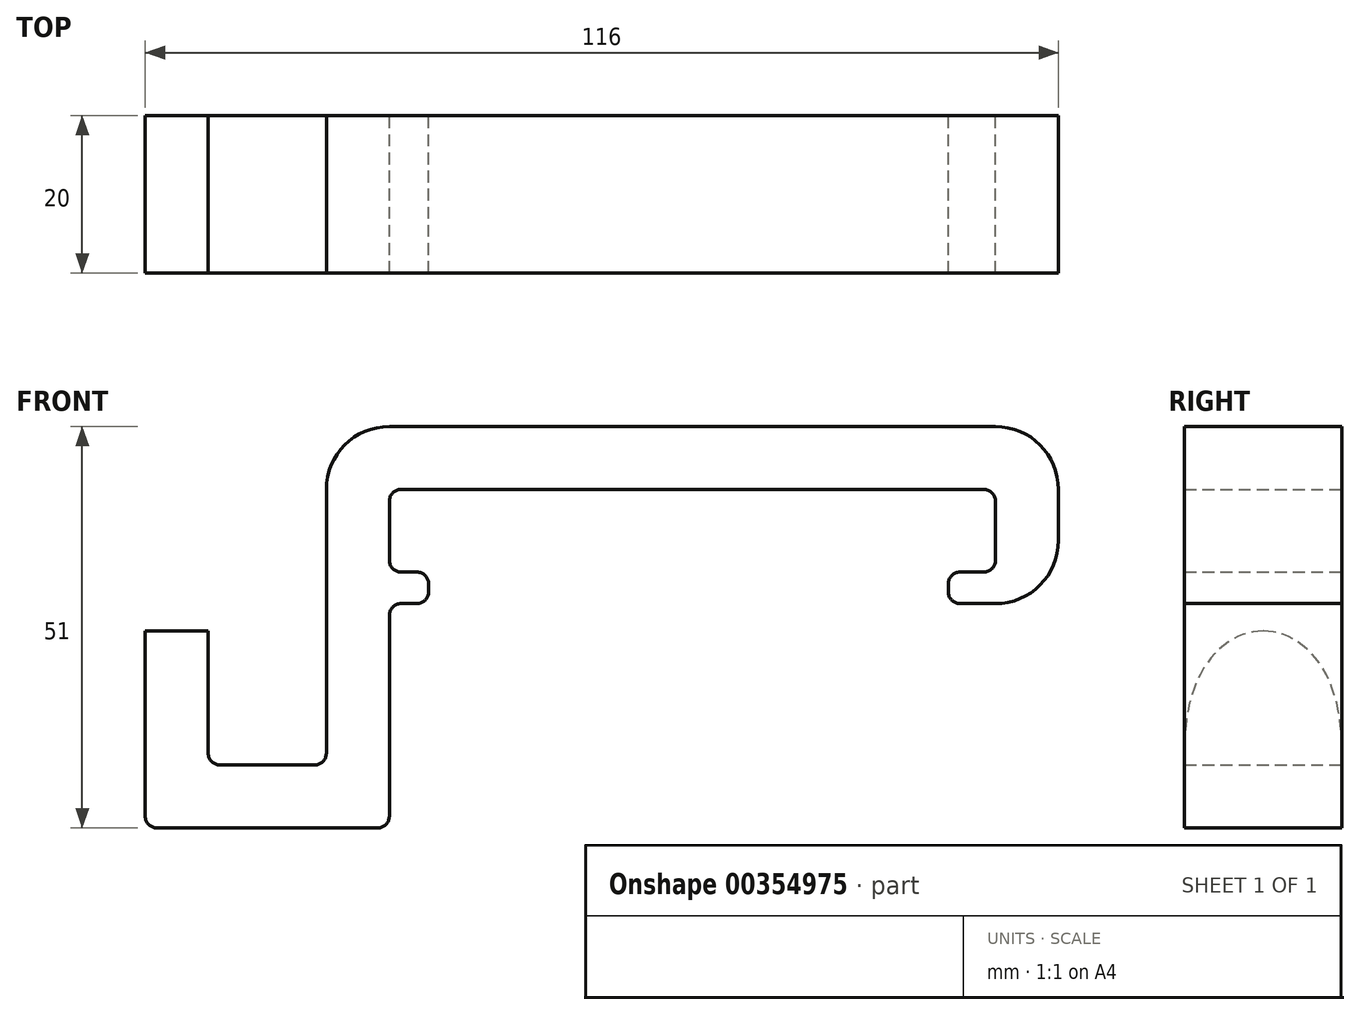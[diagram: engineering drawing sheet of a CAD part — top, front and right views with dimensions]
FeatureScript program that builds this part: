
annotation { "Feature Type Name" : "Feature", "Feature Type Description" : "" }
export const myFeature = defineFeature(function(context is Context, id is Id, definition is map)
    precondition{}
    {
        {
            var Q0;
            Q0=qCreatedBy(makeId("Front.planeOp"),FACE);
            var sketch = newSketch(context, id + "F0", { "sketchPlane" : qUnion([Q0])});
            skLineSegment(sketch, "E0", {"start": v(0, 0) * mm, "end": v(-77, 0) * mm});
            skLineSegment(sketch, "E1", {"start": v(-77, 0) * mm, "end": v(-77, -43) * mm});
            skLineSegment(sketch, "E2", {"start": v(-77, -43) * mm, "end": v(-108, -43) * mm});
            skLineSegment(sketch, "E3", {"start": v(-108, -43) * mm, "end": v(-108, -18) * mm});
            skLineSegment(sketch, "E4", {"start": v(-108, -18) * mm, "end": v(-100, -18) * mm});
            skLineSegment(sketch, "E5", {"start": v(-100, -18) * mm, "end": v(-100, -35) * mm});
            skLineSegment(sketch, "E6", {"start": v(-100, -35) * mm, "end": v(-85, -35) * mm});
            skLineSegment(sketch, "E7", {"start": v(-85, -35) * mm, "end": v(-85, 0) * mm});
            skLineSegment(sketch, "E8", {"start": v(-85, 0) * mm, "end": v(-85, 8) * mm});
            skLineSegment(sketch, "E9", {"start": v(-85, 8) * mm, "end": v(8, 8) * mm});
            skLineSegment(sketch, "E10", {"start": v(8, 8) * mm, "end": v(8, -14.5) * mm});
            skLineSegment(sketch, "E11", {"start": v(8, -14.5) * mm, "end": v(-6, -14.5) * mm});
            skLineSegment(sketch, "E12", {"start": v(-6, -14.5) * mm, "end": v(-6, -10.5) * mm});
            skLineSegment(sketch, "E13", {"start": v(-6, -10.5) * mm, "end": v(0, -10.5) * mm});
            skLineSegment(sketch, "E14", {"start": v(0, -10.5) * mm, "end": v(0, 0) * mm});
            skLineSegment(sketch, "E15", {"start": v(-77, -10.5) * mm, "end": v(-72, -10.5) * mm});
            skLineSegment(sketch, "E16", {"start": v(-72, -10.5) * mm, "end": v(-72, -14.5) * mm});
            skLineSegment(sketch, "E17", {"start": v(-72, -14.5) * mm, "end": v(-77, -14.5) * mm});
            skSolve(sketch);
        }
        {
            var Q0;
            Q0 = qSketchRegion(id + "F0", true);
            extrude(context, id + "F1", {"entities" : qUnion([Q0]), "depth" : 20 * mm});
        }
        {
            var Q0;
            Q0=makeQuery(id+"F1.opExtrude","SWEPT_EDGE",EDGE,{"disambiguationData":[OSD([sQuery(id+"F0.wireOp",EDGE,"E11"),sQuery(id+"F0.wireOp",EDGE,"E12")])]});
            var Q1;
            Q1=makeQuery(id+"F1.opExtrude","SWEPT_EDGE",EDGE,{"disambiguationData":[OSD([sQuery(id+"F0.wireOp",EDGE,"E12"),sQuery(id+"F0.wireOp",EDGE,"E13")])]});
            var Q2;
            Q2=makeQuery(id+"F1.opExtrude","SWEPT_EDGE",EDGE,{"disambiguationData":[OSD([sQuery(id+"F0.wireOp",EDGE,"E13"),sQuery(id+"F0.wireOp",EDGE,"E14")])]});
            var Q3;
            Q3=makeQuery(id+"F1.opExtrude","SWEPT_EDGE",EDGE,{"disambiguationData":[OSD([sQuery(id+"F0.wireOp",EDGE,"E0"),sQuery(id+"F0.wireOp",EDGE,"E14")])]});
            var Q4;
            Q4=makeQuery(id+"F1.opExtrude","SWEPT_EDGE",EDGE,{"disambiguationData":[OSD([sQuery(id+"F0.wireOp",EDGE,"E16"),sQuery(id+"F0.wireOp",EDGE,"E17")])]});
            var Q5;
            Q5=makeQuery(id+"F1.opExtrude","SWEPT_EDGE",EDGE,{"disambiguationData":[OSD([sQuery(id+"F0.wireOp",EDGE,"E15"),sQuery(id+"F0.wireOp",EDGE,"E16")])]});
            var Q6;
            Q6=makeQuery(id+"F1.opExtrude","SWEPT_EDGE",EDGE,{"disambiguationData":[OSD([sQuery(id+"F0.wireOp",EDGE,"E1"),sQuery(id+"F0.wireOp",EDGE,"E15")])]});
            var Q7;
            Q7=makeQuery(id+"F1.opExtrude","SWEPT_EDGE",EDGE,{"disambiguationData":[OSD([sQuery(id+"F0.wireOp",EDGE,"E1"),sQuery(id+"F0.wireOp",EDGE,"E17")])]});
            var Q8;
            Q8=makeQuery(id+"F1.opExtrude","SWEPT_EDGE",EDGE,{"disambiguationData":[OSD([sQuery(id+"F0.wireOp",EDGE,"E1"),sQuery(id+"F0.wireOp",EDGE,"E2")])]});
            var Q9;
            Q9=makeQuery(id+"F1.opExtrude","SWEPT_EDGE",EDGE,{"disambiguationData":[OSD([sQuery(id+"F0.wireOp",EDGE,"E2"),sQuery(id+"F0.wireOp",EDGE,"E3")])]});
            var Q10;
            Q10=makeQuery(id+"F1.opExtrude","SWEPT_EDGE",EDGE,{"disambiguationData":[OSD([sQuery(id+"F0.wireOp",EDGE,"E0"),sQuery(id+"F0.wireOp",EDGE,"E1")])]});
            var Q11;
            Q11=makeQuery(id+"F1.opExtrude","SWEPT_EDGE",EDGE,{"disambiguationData":[OSD([sQuery(id+"F0.wireOp",EDGE,"E6"),sQuery(id+"F0.wireOp",EDGE,"E7")])]});
            var Q12;
            Q12=makeQuery(id+"F1.opExtrude","SWEPT_EDGE",EDGE,{"disambiguationData":[OSD([sQuery(id+"F0.wireOp",EDGE,"E5"),sQuery(id+"F0.wireOp",EDGE,"E6")])]});
            fillet(context, id + "F2", {"entities" : qUnion([Q0, Q1, Q2, Q3, Q4, Q5, Q6, Q7, Q8, Q9, Q10, Q11, Q12]), "radius" : 1.5 * mm, "tangentPropagation" : true, "allowEdgeOverflow" : false});
        }
        {
            var Q0;
            Q0=makeQuery(id+"F1.opExtrude","SWEPT_FACE",FACE,{"disambiguationData":[OSD([sQuery(id+"F0.wireOp",EDGE,"E5")])]});
            var sketch = newSketch(context, id + "F3", { "sketchPlane" : qUnion([Q0])});
            skLineSegment(sketch, "E18", {"start": v(-20, -33) * mm, "end": v(-20, -18) * mm});
            skLineSegment(sketch, "E19", {"start": v(-20, -18) * mm, "end": v(0, -18) * mm});
            skLineSegment(sketch, "E20", {"start": v(0, -18) * mm, "end": v(0, -33) * mm});
            skFitSpline(sketch, "E21", {"points": [v(0, -33) * mm, v(-10, -18) * mm, v(-20, -33) * mm], "startDerivative": vector(0, 60.65) * mm, "endDerivative": vector(0, -60.65) * mm});
            skSolve(sketch);
        }
        {
            var Q0;
            Q0 = qSketchRegion(id + "F3", true);
            extrude(context, id + "F4", {"entities" : qUnion([Q0]), "operationType" : NewBodyOperationType.REMOVE, "oppositeDirection" : true, "depth" : 11 * mm});
        }
        {
            var Q0;
            Q0=makeQuery(id+"F1.opExtrude","SWEPT_EDGE",EDGE,{"disambiguationData":[OSD([sQuery(id+"F0.wireOp",EDGE,"E8"),sQuery(id+"F0.wireOp",EDGE,"E9")])]});
            var Q1;
            Q1=makeQuery(id+"F1.opExtrude","SWEPT_EDGE",EDGE,{"disambiguationData":[OSD([sQuery(id+"F0.wireOp",EDGE,"E9"),sQuery(id+"F0.wireOp",EDGE,"E10")])]});
            var Q2;
            Q2=makeQuery(id+"F1.opExtrude","SWEPT_EDGE",EDGE,{"disambiguationData":[OSD([sQuery(id+"F0.wireOp",EDGE,"E10"),sQuery(id+"F0.wireOp",EDGE,"E11")])]});
            fillet(context, id + "F5", {"entities" : qUnion([Q0, Q1, Q2]), "radius" : 8 * mm, "tangentPropagation" : true, "allowEdgeOverflow" : false});
        }
    });
